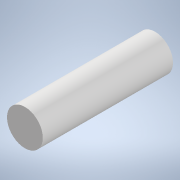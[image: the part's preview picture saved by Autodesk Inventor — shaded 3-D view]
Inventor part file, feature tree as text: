
AUTODESK INVENTOR PART (.ipt)
format: ipt  version: 2020 (Build 240168000, 168)  size: 104,960 bytes
history: native  units: in
note: dims shown in document units (in); Inventor stores cm internally (conversion verified against a paired STEP export)
features: reference x14, other x4, sketch x1, plane x1, extrude x1
ambient origin geometry x8: Origin, YZ Plane, XZ Plane, XY Plane, X Axis, Y Axis, Z Axis, Center Point
bodies: Solid1 (feature_tree)
feature tree (21):
  sketch  "Sketch2"  dims[d0=1.0in d1=0.0in]
  plane  "Work Plane1"
  extrude  "Extrusion1"  [1 undecoded]
  reference  "Reference14"
  reference  "Reference15"
  reference  "Reference16"
  reference  "Reference17"
  reference  "Reference18"
  reference  "Reference19"
  reference  "Reference20"
  reference  "Reference21"
  reference  "Reference22"
  reference  "Reference23"
  reference  "Reference24"
  reference  "Reference25"
  reference  "Reference26"
  reference  "Reference27"
  other  "<userpath>\Documents\Inventor\Drone\Assembly.iam"
  other  "Assembly.iam"
  other  "Frame:1"
  other  "F330 low plate v1:1"
note: 1 required parameter value undecoded (feature->parameter linkage not recoverable at this tier; creation-order binding heuristic only, values carry confidence <= 0.55)
